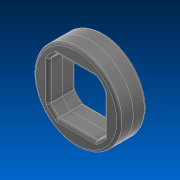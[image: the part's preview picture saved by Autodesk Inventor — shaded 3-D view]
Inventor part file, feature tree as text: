
AUTODESK INVENTOR PART (.ipt)
format: ipt  version: 2022.2 (Build 262287000, 287)  size: 195,072 bytes
history: native  units: in
note: dims shown in document units (in); Inventor stores cm internally (conversion verified against a paired STEP export)
features: fillet x1
ambient origin geometry x8: Origin, YZ Plane, XZ Plane, XY Plane, X Axis, Y Axis, Z Axis, Center Point
bodies: Solid1 (feature_tree)
feature tree (1):
  fillet  "Fillet1"  [1 undecoded]
note: 1 required parameter value undecoded (feature->parameter linkage not recoverable at this tier; creation-order binding heuristic only, values carry confidence <= 0.55)
